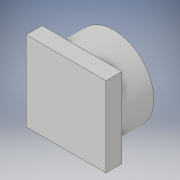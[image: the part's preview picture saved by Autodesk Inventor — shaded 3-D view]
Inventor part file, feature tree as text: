
AUTODESK INVENTOR PART (.ipt)
format: ipt  version: 2018 (Build 220112000, 112)  size: 103,936 bytes
history: native  units: mm
features: extrude x2, sketch x2
ambient origin geometry x8: Origin, YZ Plane, XZ Plane, XY Plane, X Axis, Y Axis, Z Axis, Center Point
bodies: Volumenkörper1 (feature_tree)
feature tree (4):
  extrude  "Extrusion1"  Depth=20.0mm TaperAngle=0.0deg
  extrude  "Extrusion2"  [1 undecoded]
  sketch  "Skizze1"  dims[d0=50.0mm d1=20.0mm d2=0.0mm]
  sketch  "Skizze2"  dims[d3=10.0mm d4=0.0mm]
note: 1 required parameter value undecoded (feature->parameter linkage not recoverable at this tier; creation-order binding heuristic only, values carry confidence <= 0.55)
